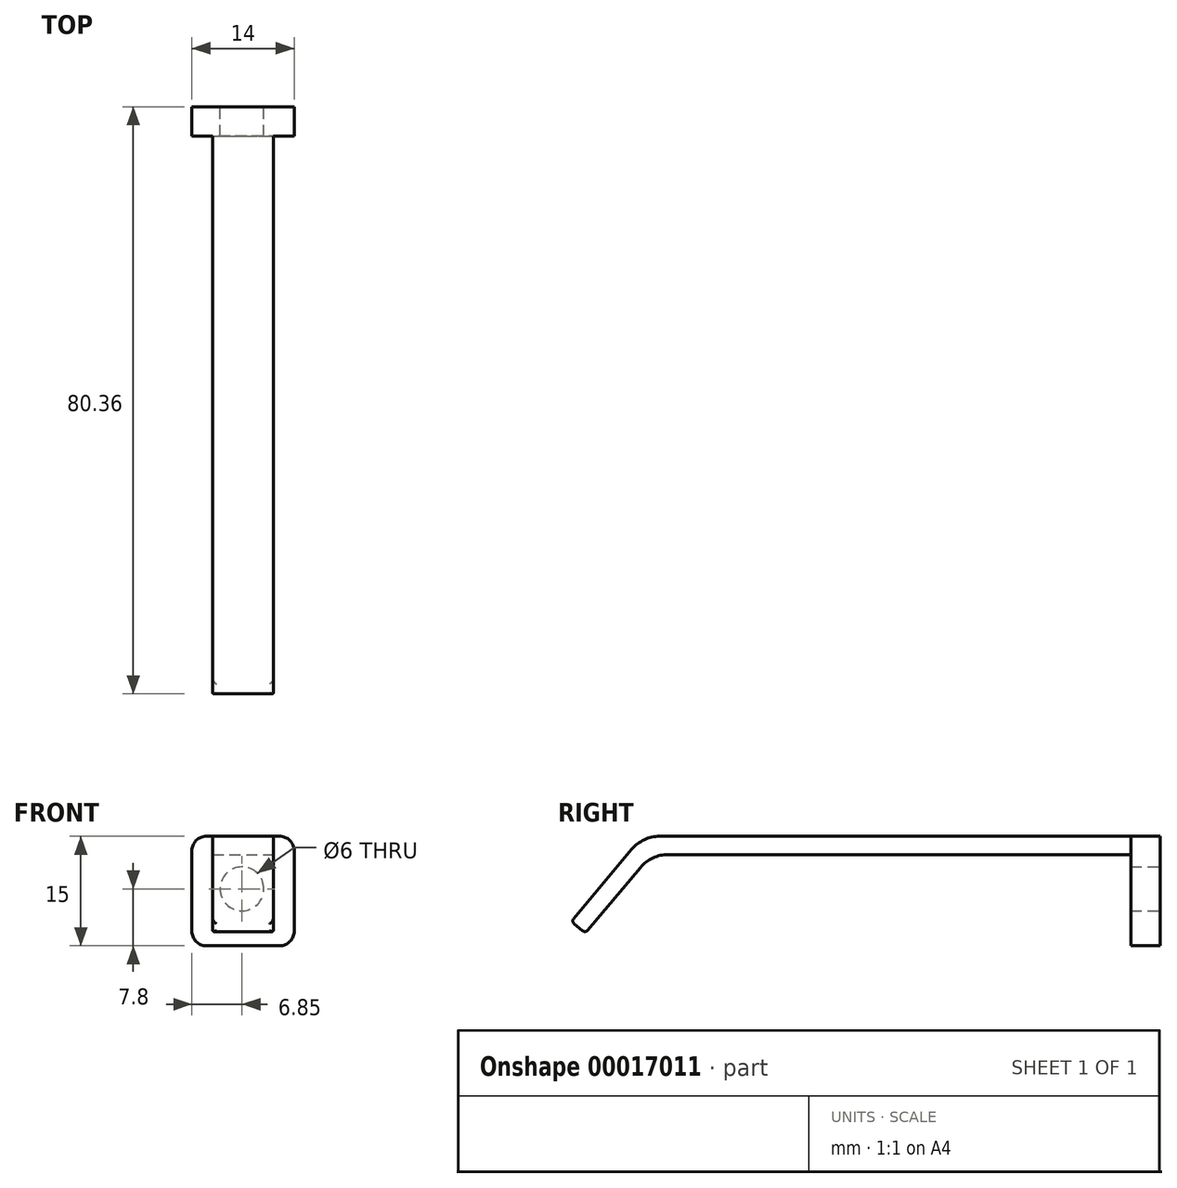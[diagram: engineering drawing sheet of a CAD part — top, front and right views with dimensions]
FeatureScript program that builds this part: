
annotation { "Feature Type Name" : "Feature", "Feature Type Description" : "" }
export const myFeature = defineFeature(function(context is Context, id is Id, definition is map)
    precondition{}
    {
        {
            var Q0;
            Q0=qCreatedBy(makeId("Front.planeOp"),FACE);
            var sketch = newSketch(context, id + "F0", { "sketchPlane" : qUnion([Q0])});
            skLineSegment(sketch, "E0.bottom", {"start": v(-8.3, 0) * mm, "end": v(0, 0) * mm});
            skLineSegment(sketch, "E0.top", {"start": v(-8.3, 2.5) * mm, "end": v(0, 2.5) * mm});
            skLineSegment(sketch, "E0.left", {"start": v(-8.3, 0) * mm, "end": v(-8.3, 2.5) * mm});
            skLineSegment(sketch, "E0.right", {"start": v(0, 0) * mm, "end": v(0, 2.5) * mm});
            skSolve(sketch);
        }
        {
            var Q0;
            Q0=makeQuery(id+"F0.imprint","IMPRINT",FACE,{"disambiguationData":[TD([[makeQuery(id+"F0.imprint","IMPRINT",EDGE,{"derivedFrom":sQuery(id+"F0.wireOp",EDGE,"E0.bottom")}),1.0]])]});
            extrude(context, id + "F1", {"entities" : qUnion([Q0]), "depth" : 66.8 * mm});
        }
        {
            var Q0;
            Q0=makeQuery(id+"F1.opExtrude","CAP_FACE",FACE,{"disambiguationData":[OSD([sQuery(id+"F0.wireOp",EDGE,"E0.bottom"),sQuery(id+"F0.wireOp",EDGE,"E0.top"),sQuery(id+"F0.wireOp",EDGE,"E0.left"),sQuery(id+"F0.wireOp",EDGE,"E0.right")])],"isStart":true});
            var sketch = newSketch(context, id + "F2", { "sketchPlane" : qUnion([Q0])});
            skLineSegment(sketch, "E1.bottom", {"start": v(-2.85, 2.5) * mm, "end": v(11.15, 2.5) * mm});
            skLineSegment(sketch, "E1.top", {"start": v(-2.85, -12.5) * mm, "end": v(11.15, -12.5) * mm});
            skLineSegment(sketch, "E1.left", {"start": v(-2.85, 2.5) * mm, "end": v(-2.85, -12.5) * mm});
            skLineSegment(sketch, "E1.right", {"start": v(11.15, 2.5) * mm, "end": v(11.15, -12.5) * mm});
            skSolve(sketch);
        }
        {
            var Q0;
            Q0=makeQuery(id+"F2.imprint","IMPRINT",FACE,{"disambiguationData":[TD([[makeQuery(id+"F2.imprint","IMPRINT",EDGE,{"derivedFrom":sQuery(id+"F2.wireOp",EDGE,"E1.top")}),1.0]])]});
            var Q1;
            Q1=makeQuery(id+"F2.imprint","IMPRINT",FACE,{"disambiguationData":[TD([[makeQuery(id+"F2.imprint","IMPRINT",EDGE,{"derivedFrom":makeQuery(id+"F1.opExtrude","CAP_EDGE",EDGE,{"disambiguationData":[OSD([sQuery(id+"F0.wireOp",EDGE,"E0.bottom")])],"isStart":true})}),-1.0]])]});
            extrude(context, id + "F3", {"entities" : qUnion([Q0, Q1]), "operationType" : NewBodyOperationType.ADD, "depth" : 4 * mm});
        }
        {
            var Q0;
            Q0=makeQuery(id+"F3.opExtrude","SWEPT_EDGE",EDGE,{"disambiguationData":[OSD([sQuery(id+"F2.wireOp",EDGE,"E1.bottom"),sQuery(id+"F2.wireOp",EDGE,"E1.left")])]});
            var Q1;
            Q1=makeQuery(id+"F3.opExtrude","SWEPT_EDGE",EDGE,{"disambiguationData":[OSD([sQuery(id+"F2.wireOp",EDGE,"E1.bottom"),sQuery(id+"F2.wireOp",EDGE,"E1.right")])]});
            var Q2;
            Q2=makeQuery(id+"F3.opExtrude","SWEPT_EDGE",EDGE,{"disambiguationData":[OSD([sQuery(id+"F2.wireOp",EDGE,"E1.top"),sQuery(id+"F2.wireOp",EDGE,"E1.right")])]});
            var Q3;
            Q3=makeQuery(id+"F3.opExtrude","SWEPT_EDGE",EDGE,{"disambiguationData":[OSD([sQuery(id+"F2.wireOp",EDGE,"E1.top"),sQuery(id+"F2.wireOp",EDGE,"E1.left")])]});
            fillet(context, id + "F4", {"entities" : qUnion([Q0, Q1, Q2, Q3]), "radius" : 2 * mm, "tangentPropagation" : true, "allowEdgeOverflow" : false});
        }
        {
            var Q0;
            Q0=makeQuery(id+"F1.opExtrude","SWEPT_FACE",FACE,{"disambiguationData":[OSD([sQuery(id+"F0.wireOp",EDGE,"E0.left")])]});
            var sketch = newSketch(context, id + "F5", { "sketchPlane" : qUnion([Q0])});
            skLineSegment(sketch, "E2", {"start": v(66.8, 2.5) * mm, "end": v(76.56, -9.14) * mm});
            skLineSegment(sketch, "E3", {"start": v(76.56, -9.14) * mm, "end": v(74.65, -10.75) * mm});
            skLineSegment(sketch, "E4", {"start": v(74.65, -10.75) * mm, "end": v(64.87, 0.9) * mm});
            skLineSegment(sketch, "E5", {"start": v(64.87, 0.9) * mm, "end": v(66.8, 2.5) * mm});
            skSolve(sketch);
        }
        {
            var Q0;
            Q0 = qSketchRegion(id + "F5", true);
            extrude(context, id + "F6", {"entities" : qUnion([Q0]), "operationType" : NewBodyOperationType.ADD, "oppositeDirection" : true, "depth" : 8.3 * mm});
        }
        {
            var Q0;
            {var subQ0=sQuery(id+"F0.wireOp",EDGE,"E0.top");Q0=makeQuery(id+"F6.boolean.opBoolean","MERGE",EDGE,{"derivedFrom":[makeQuery(id+"F1.opExtrude","CAP_EDGE",EDGE,{"disambiguationData":[OSD([subQ0])],"isStart":false}),makeQuery(id+"F6.opExtrude","SWEPT_EDGE",EDGE,{"disambiguationData":[OSD([subQ0,sQuery(id+"F0.wireOp",EDGE,"E0.left"),sQuery(id+"F5.wireOp",EDGE,"E2"),sQuery(id+"F5.wireOp",EDGE,"E5")])]})]});}
            fillet(context, id + "F7", {"entities" : qUnion([Q0]), "radius" : 5 * mm, "tangentPropagation" : true, "allowEdgeOverflow" : false});
        }
        {
            var Q0;
            Q0=makeQuery(id+"F6.boolean.opBoolean","INTERSECT",EDGE,{"derivedFrom":[makeQuery(id+"F1.opExtrude","SWEPT_FACE",FACE,{"disambiguationData":[OSD([sQuery(id+"F0.wireOp",EDGE,"E0.bottom")])]}),makeQuery(id+"F6.opExtrude","SWEPT_FACE",FACE,{"disambiguationData":[OSD([sQuery(id+"F5.wireOp",EDGE,"E4")])]})]});
            fillet(context, id + "F8", {"entities" : qUnion([Q0]), "radius" : 5 * mm, "tangentPropagation" : true, "allowEdgeOverflow" : false});
        }
        {
            var Q0;
            Q0=makeQuery(id+"F6.opExtrude","CAP_EDGE",EDGE,{"disambiguationData":[OSD([sQuery(id+"F5.wireOp",EDGE,"E3")])],"isStart":true});
            var Q1;
            Q1=makeQuery(id+"F6.opExtrude","CAP_EDGE",EDGE,{"disambiguationData":[OSD([sQuery(id+"F5.wireOp",EDGE,"E3")])],"isStart":false});
            var Q2;
            Q2=makeQuery(id+"F6.opExtrude","SWEPT_EDGE",EDGE,{"disambiguationData":[OSD([sQuery(id+"F5.wireOp",EDGE,"E2"),sQuery(id+"F5.wireOp",EDGE,"E3")])]});
            var Q3;
            Q3=makeQuery(id+"F6.opExtrude","SWEPT_EDGE",EDGE,{"disambiguationData":[OSD([sQuery(id+"F5.wireOp",EDGE,"E3"),sQuery(id+"F5.wireOp",EDGE,"E4")])]});
            fillet(context, id + "F9", {"entities" : qUnion([Q0, Q1, Q2, Q3]), "radius" : 0.5 * mm, "tangentPropagation" : true, "allowEdgeOverflow" : false});
        }
        {
            var Q0;
            Q0=makeQuery(id+"F3.opExtrude","CAP_FACE",FACE,{"disambiguationData":[OSD([sQuery(id+"F2.wireOp",EDGE,"E1.bottom"),sQuery(id+"F2.wireOp",EDGE,"E1.top"),sQuery(id+"F2.wireOp",EDGE,"E1.left"),sQuery(id+"F2.wireOp",EDGE,"E1.right")])],"isStart":false});
            var sketch = newSketch(context, id + "F10", { "sketchPlane" : qUnion([Q0])});
            skCircle(sketch, "E6", {"center": v(4.3, -4.7) * mm, "radius": 3 * mm});
            skSolve(sketch);
        }
        {
            var Q0;
            Q0 = qSketchRegion(id + "F10", true);
            extrude(context, id + "F11", {"entities" : qUnion([Q0]), "operationType" : NewBodyOperationType.REMOVE, "oppositeDirection" : true, "depth" : 25 * mm});
        }
    });
